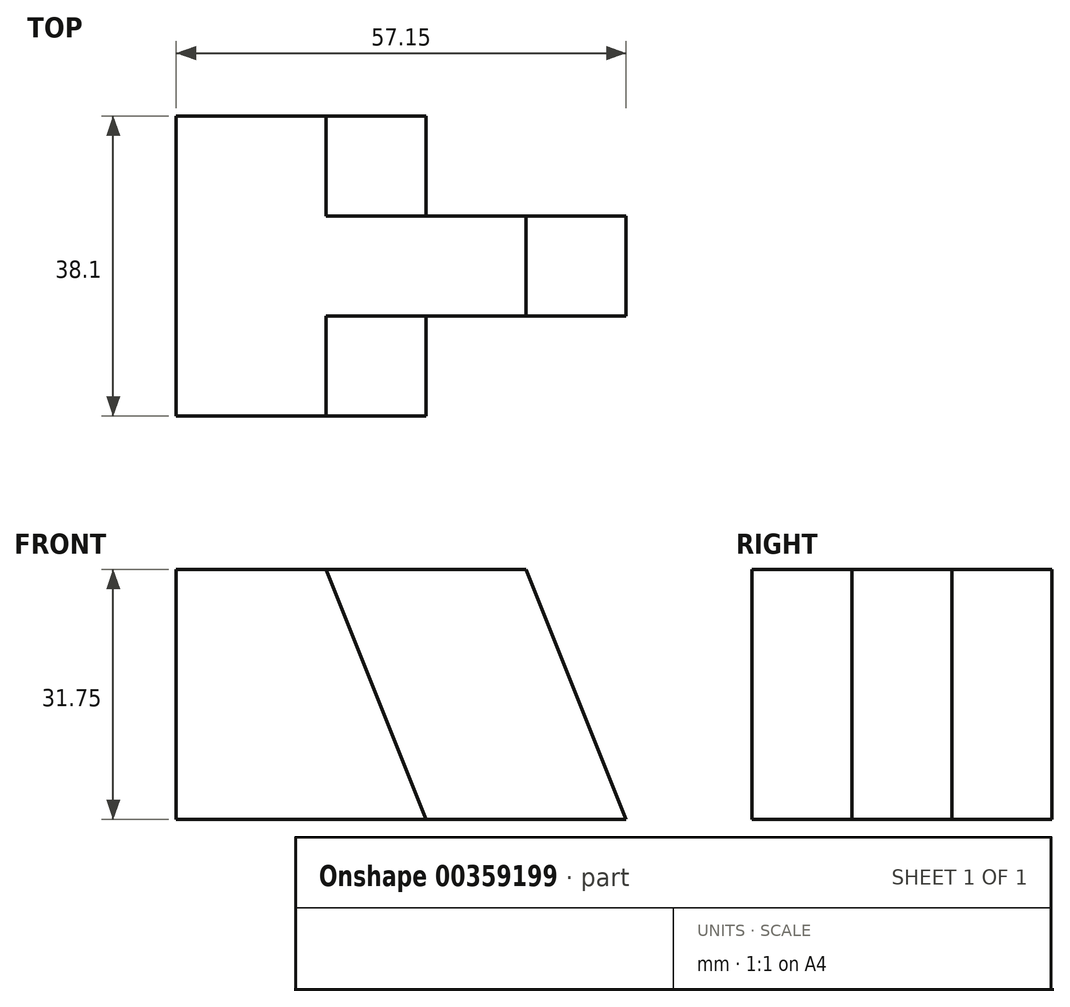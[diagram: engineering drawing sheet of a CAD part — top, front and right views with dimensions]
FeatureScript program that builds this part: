
annotation { "Feature Type Name" : "Feature", "Feature Type Description" : "" }
export const myFeature = defineFeature(function(context is Context, id is Id, definition is map)
    precondition{}
    {
        {
            var Q0;
            Q0=qCreatedBy(makeId("Top.planeOp"),FACE);
            var sketch = newSketch(context, id + "F0", { "sketchPlane" : qUnion([Q0])});
            skLineSegment(sketch, "E0", {"start": v(0, 38.1) * mm, "end": v(0, 0) * mm});
            skLineSegment(sketch, "E1", {"start": v(0, 0) * mm, "end": v(31.75, 0) * mm});
            skLineSegment(sketch, "E2", {"start": v(31.75, 0) * mm, "end": v(31.75, 12.7) * mm});
            skLineSegment(sketch, "E3", {"start": v(31.75, 12.7) * mm, "end": v(57.15, 12.7) * mm});
            skLineSegment(sketch, "E4", {"start": v(0, 38.1) * mm, "end": v(31.75, 38.1) * mm});
            skLineSegment(sketch, "E5", {"start": v(31.75, 38.1) * mm, "end": v(31.75, 25.4) * mm});
            skLineSegment(sketch, "E6", {"start": v(31.75, 25.4) * mm, "end": v(57.15, 25.4) * mm});
            skLineSegment(sketch, "E7", {"start": v(57.15, 25.4) * mm, "end": v(57.15, 12.7) * mm});
            skSolve(sketch);
        }
        {
            var Q0;
            Q0=makeQuery(id+"F0.imprint","IMPRINT",FACE,{"disambiguationData":[TD([[makeQuery(id+"F0.imprint","IMPRINT",EDGE,{"derivedFrom":sQuery(id+"F0.wireOp",EDGE,"E0")}),1.0]])]});
            extrude(context, id + "F1", {"entities" : qUnion([Q0]), "depth" : 31.75 * mm});
        }
        {
            var Q0;
            Q0=makeQuery(id+"F1.opExtrude","SWEPT_FACE",FACE,{"disambiguationData":[OSD([sQuery(id+"F0.wireOp",EDGE,"E1")])]});
            var sketch = newSketch(context, id + "F2", { "sketchPlane" : qUnion([Q0])});
            skLineSegment(sketch, "E8", {"start": v(19.05, 31.75) * mm, "end": v(31.75, 0) * mm});
            skLineSegment(sketch, "E9", {"start": v(31.75, 0) * mm, "end": v(31.75, 31.75) * mm});
            skLineSegment(sketch, "E10", {"start": v(31.75, 31.75) * mm, "end": v(19.05, 31.75) * mm});
            skSolve(sketch);
        }
        {
            var Q0;
            Q0 = qSketchRegion(id + "F2", true);
            extrude(context, id + "F3", {"entities" : qUnion([Q0]), "operationType" : NewBodyOperationType.REMOVE, "oppositeDirection" : true, "depth" : 12.7 * mm});
        }
        {
            var Q0;
            Q0=makeQuery(id+"F3.boolean.opBoolean","MERGE",FACE,{"derivedFrom":[makeQuery(id+"F1.opExtrude","SWEPT_FACE",FACE,{"disambiguationData":[OSD([sQuery(id+"F0.wireOp",EDGE,"E3")])]}),makeQuery(id+"F3.opExtrude","CAP_FACE",FACE,{"disambiguationData":[OSD([sQuery(id+"F2.wireOp",EDGE,"E8"),sQuery(id+"F2.wireOp",EDGE,"E9"),sQuery(id+"F2.wireOp",EDGE,"E10")])],"isStart":false})]});
            var sketch = newSketch(context, id + "F4", { "sketchPlane" : qUnion([Q0])});
            skLineSegment(sketch, "E11", {"start": v(44.45, 31.75) * mm, "end": v(57.15, 0) * mm});
            skLineSegment(sketch, "E12", {"start": v(57.15, 0) * mm, "end": v(57.15, 31.75) * mm});
            skLineSegment(sketch, "E13", {"start": v(57.15, 31.75) * mm, "end": v(44.45, 31.75) * mm});
            skSolve(sketch);
        }
        {
            var Q0;
            Q0 = qSketchRegion(id + "F4", true);
            extrude(context, id + "F5", {"entities" : qUnion([Q0]), "operationType" : NewBodyOperationType.REMOVE, "oppositeDirection" : true, "depth" : 12.7 * mm});
        }
        {
            var Q0;
            Q0=makeQuery(id+"F1.opExtrude","SWEPT_FACE",FACE,{"disambiguationData":[OSD([sQuery(id+"F0.wireOp",EDGE,"E4")])]});
            var sketch = newSketch(context, id + "F6", { "sketchPlane" : qUnion([Q0])});
            skLineSegment(sketch, "E14", {"start": v(-31.75, 31.75) * mm, "end": v(-31.75, 0) * mm});
            skLineSegment(sketch, "E15", {"start": v(-31.75, 0) * mm, "end": v(-19.05, 31.75) * mm});
            skLineSegment(sketch, "E16", {"start": v(-19.05, 31.75) * mm, "end": v(-31.75, 31.75) * mm});
            skSolve(sketch);
        }
        {
            var Q0;
            Q0=makeQuery(id+"F6.imprint","IMPRINT",FACE,{"disambiguationData":[TD([[makeQuery(id+"F6.imprint","IMPRINT",EDGE,{"derivedFrom":sQuery(id+"F6.wireOp",EDGE,"E14")}),1.0]])]});
            extrude(context, id + "F7", {"entities" : qUnion([Q0]), "operationType" : NewBodyOperationType.REMOVE, "oppositeDirection" : true, "depth" : 12.7 * mm});
        }
    });
